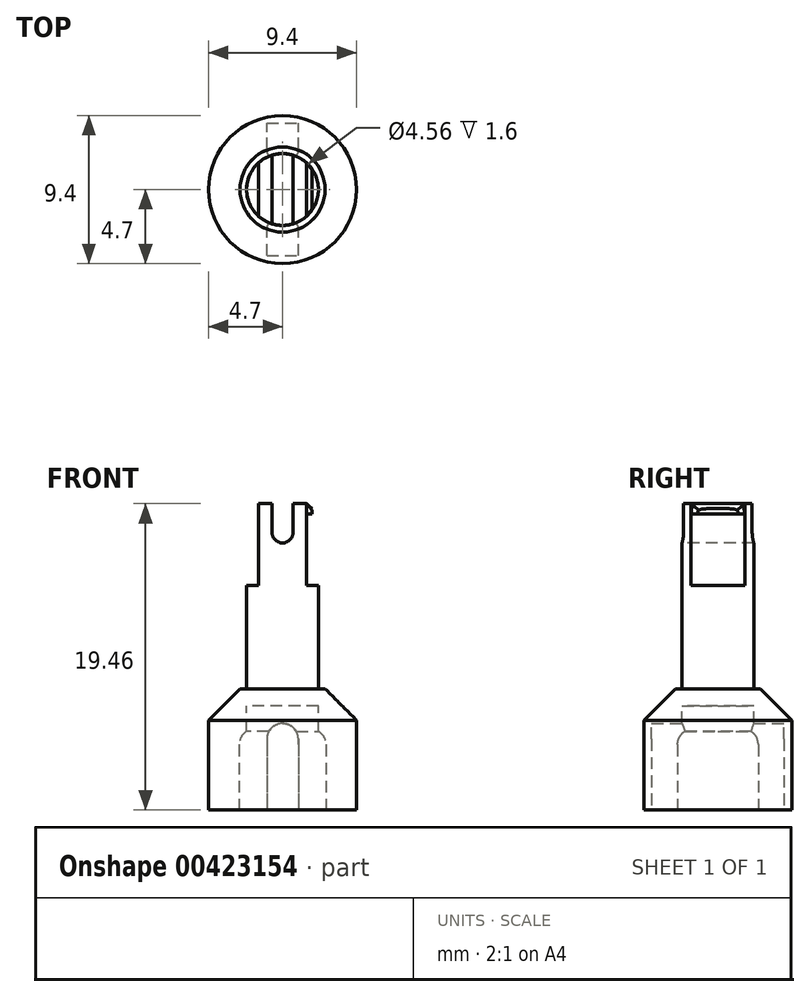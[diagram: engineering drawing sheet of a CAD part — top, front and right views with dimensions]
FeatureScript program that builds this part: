
annotation { "Feature Type Name" : "Feature", "Feature Type Description" : "" }
export const myFeature = defineFeature(function(context is Context, id is Id, definition is map)
    precondition{}
    {
        {
            assignVariable(context, id + "F0", {"variableType" : VariableType.LENGTH, "name" : "dogbone_cutout", "lengthValue" : 5.5 * mm});
        }
        {
            assignVariable(context, id + "F1", {"variableType" : VariableType.LENGTH, "name" : "shaft_length", "lengthValue" : 11.76 * mm});
        }
        {
            assignVariable(context, id + "F2", {"variableType" : VariableType.LENGTH, "name" : "outdrive_length", "lengthValue" : 7.7 * mm});
        }
        {
            assignVariable(context, id + "F3", {"variableType" : VariableType.LENGTH, "name" : "outdrive_depth", "lengthValue" : 6.6 * mm});
        }
        {
            assignVariable(context, id + "F4", {"variableType" : VariableType.LENGTH, "name" : "shaft_flat_length", "lengthValue" : 5.2 * mm});
        }
        {
            assignVariable(context, id + "F5", {"variableType" : VariableType.LENGTH, "name" : "flat_cutout_width", "lengthValue" : 1.35 * mm});
        }
        {
            assignVariable(context, id + "F6", {"variableType" : VariableType.LENGTH, "name" : "flat_cutout_depth", "lengthValue" : 2.5 * mm});
        }
        {
            assignVariable(context, id + "F7", {"variableType" : VariableType.LENGTH, "name" : "chamfer_length", "lengthValue" : 2 * mm});
        }
        {
            var Q0;
            Q0=qCreatedBy(makeId("Top.planeOp"),FACE);
            var sketch = newSketch(context, id + "F8", { "sketchPlane" : qUnion([Q0])});
            skCircle(sketch, "E0", {"center": v(0, 0) * mm, "radius": 4.7 * mm});
            skCircle(sketch, "E1", {"center": v(0, 0) * mm, "radius": 2.28 * mm});
            skSolve(sketch);
        }
        {
            var Q0;
            Q0=makeQuery(id+"F8.imprint","IMPRINT",FACE,{"disambiguationData":[TD([[makeQuery(id+"F8.imprint","IMPRINT",EDGE,{"derivedFrom":sQuery(id+"F8.wireOp",EDGE,"E1")}),1.0]])]});
            extrude(context, id + "F9", {"entities" : qUnion([Q0]), "depth" : getVariable(context, 'shaft_length'), "offsetDistance" : 25 * mm, "hasSecondDirection" : true, "secondDirectionOppositeDirection" : true, "secondDirectionDepth" : getVariable(context, 'outdrive_length') - getVariable(context, 'outdrive_depth')});
        }
        {
            var Q0;
            Q0=makeQuery(id+"F8.imprint","IMPRINT",FACE,{"disambiguationData":[TD([[makeQuery(id+"F8.imprint","IMPRINT",EDGE,{"derivedFrom":sQuery(id+"F8.wireOp",EDGE,"E0")}),1.0]])]});
            extrude(context, id + "F10", {"entities" : qUnion([Q0]), "operationType" : NewBodyOperationType.ADD, "oppositeDirection" : true, "depth" : getVariable(context, 'outdrive_length'), "offsetDistance" : 25 * mm});
        }
        {
            var Q0;
            Q0=makeQuery(id+"F10.opExtrude","CAP_EDGE",EDGE,{"disambiguationData":[OSD([sQuery(id+"F8.wireOp",EDGE,"E0")])],"isStart":true});
            chamfer(context, id + "F11", {"entities" : qUnion([Q0]), "width" : getVariable(context, 'chamfer_length'), "tangentPropagation" : true});
        }
        {
            var Q0;
            Q0=makeQuery(id+"F9.opExtrude","CAP_FACE",FACE,{"disambiguationData":[OSD([sQuery(id+"F8.wireOp",EDGE,"E1")])],"isStart":false});
            var sketch = newSketch(context, id + "F12", { "sketchPlane" : qUnion([Q0])});
            skLineSegment(sketch, "E2.bottom", {"start": v(1.51, 4.45) * mm, "end": v(-1.51, 4.45) * mm, "construction": true});
            skLineSegment(sketch, "E2.top", {"start": v(1.51, -4.45) * mm, "end": v(-1.51, -4.45) * mm, "construction": true});
            skLineSegment(sketch, "E2.left", {"start": v(1.51, 4.45) * mm, "end": v(1.51, -4.45) * mm});
            skLineSegment(sketch, "E2.right", {"start": v(-1.51, 4.45) * mm, "end": v(-1.51, -4.45) * mm});
            skPoint(sketch, "E2.middle", {"position": v(0, 0) * mm});
            skLineSegment(sketch, "E3", {"start": v(1.51, 4.45) * mm, "end": v(3.52, 4.45) * mm});
            skLineSegment(sketch, "E4", {"start": v(3.52, 4.45) * mm, "end": v(3.52, -4.43) * mm});
            skLineSegment(sketch, "E5", {"start": v(3.52, -4.43) * mm, "end": v(1.51, -4.45) * mm});
            skLineSegment(sketch, "E6.MirrorCS", {"start": v(-1.51, 4.45) * mm, "end": v(-3.52, 4.45) * mm});
            skLineSegment(sketch, "E7.MirrorCS", {"start": v(-3.52, 4.45) * mm, "end": v(-3.52, -4.43) * mm});
            skLineSegment(sketch, "E8.MirrorCS", {"start": v(-3.52, -4.43) * mm, "end": v(-1.51, -4.45) * mm});
            skSolve(sketch);
        }
        {
            var Q0;
            Q0 = qSketchRegion(id + "F12", true);
            extrude(context, id + "F13", {"entities" : qUnion([Q0]), "operationType" : NewBodyOperationType.REMOVE, "oppositeDirection" : true, "depth" : getVariable(context, 'shaft_flat_length'), "offsetDistance" : 25 * mm});
        }
        {
            var Q0;
            Q0=makeQuery(id+"F9.opExtrude","CAP_FACE",FACE,{"disambiguationData":[OSD([sQuery(id+"F8.wireOp",EDGE,"E1")])],"isStart":false});
            var sketch = newSketch(context, id + "F14", { "sketchPlane" : qUnion([Q0])});
            skLineSegment(sketch, "E9.bottom", {"start": v(-0.68, 4.65) * mm, "end": v(0.68, 4.65) * mm});
            skLineSegment(sketch, "E9.top", {"start": v(-0.68, -4.65) * mm, "end": v(0.68, -4.65) * mm});
            skLineSegment(sketch, "E9.left", {"start": v(-0.68, 4.65) * mm, "end": v(-0.68, -4.65) * mm});
            skLineSegment(sketch, "E9.right", {"start": v(0.68, 4.65) * mm, "end": v(0.68, -4.65) * mm});
            skPoint(sketch, "E9.middle", {"position": v(0, 0) * mm});
            skSolve(sketch);
        }
        {
            var Q0;
            Q0 = qSketchRegion(id + "F14", true);
            extrude(context, id + "F15", {"entities" : qUnion([Q0]), "operationType" : NewBodyOperationType.REMOVE, "oppositeDirection" : true, "depth" : getVariable(context, 'flat_cutout_depth'), "offsetDistance" : 25 * mm});
        }
        {
            var Q0;
            Q0=makeQuery(id+"F15.boolean.opBoolean","COPY",EDGE,{"derivedFrom":makeQuery(id+"F15.opExtrude","CAP_EDGE",EDGE,{"disambiguationData":[OSD([sQuery(id+"F14.wireOp",EDGE,"E9.left")])],"isStart":false})});
            var Q1;
            Q1=makeQuery(id+"F15.boolean.opBoolean","COPY",EDGE,{"derivedFrom":makeQuery(id+"F15.opExtrude","CAP_EDGE",EDGE,{"disambiguationData":[OSD([sQuery(id+"F14.wireOp",EDGE,"E9.right")])],"isStart":false})});
            fillet(context, id + "F16", {"entities" : qUnion([Q0, Q1]), "tangentPropagation" : true, "radius" : getVariable(context, 'flat_cutout_width') / 2, "defaultsChanged" : false, "vertexSettings" : [], "allowEdgeOverflow" : false});
        }
        {
            assignVariable(context, id + "F17", {"variableType" : VariableType.LENGTH, "name" : "flat_bump_offset", "lengthValue" : 0.65 * mm});
        }
        {
            var Q0;
            {var subQ0=sQuery(id+"F8.wireOp",EDGE,"E1");Q0=makeQuery(id+"F15.boolean.opBoolean","SPLIT",FACE,{"disambiguationData":[TD([makeQuery(id+"F13.boolean.opBoolean","COPY",FACE,{"derivedFrom":makeQuery(id+"F13.opExtrude","SWEPT_FACE",FACE,{"disambiguationData":[OSD([sQuery(id+"F12.wireOp",EDGE,"E2.left")])]})})])],"derivedFrom":makeQuery(id+"F9.opExtrude","CAP_FACE",FACE,{"disambiguationData":[OSD([subQ0])],"isStart":false})});}
            cPlane(context, id + "F18", {"entities" : qUnion([Q0]), "cplaneType" : CPlaneType.OFFSET, "offset" : getVariable(context, 'flat_bump_offset'), "oppositeDirection" : true, "width" : 150 * mm, "height" : 150 * mm});
        }
        {
            var Q0;
            Q0=qCreatedBy(id+"F18.planeOp",FACE);
            var sketch = newSketch(context, id + "F19", { "sketchPlane" : qUnion([Q0])});
            skArc(sketch, "E10", {"start": v(0.67, -2.18) * mm, "mid": v(2.28, 0) * mm, "end": v(0.68, 2.18) * mm});
            skLineSegment(sketch, "E11", {"start": v(0.67, 2.18) * mm, "end": v(0.68, -2.18) * mm});
            skArc(sketch, "E12.MirrorCS", {"start": v(-0.67, -2.18) * mm, "mid": v(-2.28, 0) * mm, "end": v(-0.68, 2.18) * mm});
            skLineSegment(sketch, "E13.MirrorCS", {"start": v(-0.67, 2.18) * mm, "end": v(-0.68, -2.18) * mm});
            skSolve(sketch);
        }
        {
            var Q0;
            Q0=makeQuery(id+"F19.imprint","IMPRINT",FACE,{"disambiguationData":[TD([[makeQuery(id+"F19.imprint","IMPRINT",EDGE,{"derivedFrom":sQuery(id+"F19.wireOp",EDGE,"E10")}),1.0]])]});
            var Q1;
            {var subQ0=sQuery(id+"F8.wireOp",EDGE,"E1");Q1=makeQuery(id+"F15.boolean.opBoolean","SPLIT",FACE,{"disambiguationData":[TD([makeQuery(id+"F13.boolean.opBoolean","COPY",FACE,{"derivedFrom":makeQuery(id+"F13.opExtrude","SWEPT_FACE",FACE,{"disambiguationData":[OSD([sQuery(id+"F12.wireOp",EDGE,"E2.left")])]})})])],"derivedFrom":makeQuery(id+"F9.opExtrude","CAP_FACE",FACE,{"disambiguationData":[OSD([subQ0])],"isStart":false})});}
            loft(context, id + "F20", {"operationType" : NewBodyOperationType.ADD, "sheetProfilesArray" : [{ "sheetProfileEntities" : qUnion([Q0]) }, { "sheetProfileEntities" : qUnion([Q1]) }]});
        }
        {
            var Q0;
            Q0=qCreatedBy(id+"F18.planeOp",FACE);
            var sketch = newSketch(context, id + "F21", { "sketchPlane" : qUnion([Q0])});
            skLineSegment(sketch, "E14.bottom", {"start": v(2.28, 1.95) * mm, "end": v(1.86, 1.95) * mm});
            skLineSegment(sketch, "E14.top", {"start": v(2.28, -1.95) * mm, "end": v(1.86, -1.95) * mm});
            skLineSegment(sketch, "E14.left", {"start": v(2.28, 1.95) * mm, "end": v(2.28, -1.95) * mm});
            skLineSegment(sketch, "E14.right", {"start": v(1.86, 1.95) * mm, "end": v(1.86, -1.95) * mm});
            skLineSegment(sketch, "E15.MirrorCS", {"start": v(-1.86, 1.95) * mm, "end": v(-1.86, -1.95) * mm});
            skLineSegment(sketch, "E16.MirrorCS", {"start": v(-2.28, 1.95) * mm, "end": v(-1.86, 1.95) * mm});
            skLineSegment(sketch, "E17.MirrorCS", {"start": v(-2.28, 1.95) * mm, "end": v(-2.28, -1.95) * mm});
            skLineSegment(sketch, "E18.MirrorCS", {"start": v(-2.28, -1.95) * mm, "end": v(-1.86, -1.95) * mm});
            skSolve(sketch);
        }
        {
            var Q0;
            Q0 = qSketchRegion(id + "F21", true);
            extrude(context, id + "F22", {"entities" : qUnion([Q0]), "operationType" : NewBodyOperationType.REMOVE, "depth" : 25 * mm, "offsetDistance" : 25 * mm});
        }
        {
            assignVariable(context, id + "F23", {"variableType" : VariableType.LENGTH, "name" : "dogbone_pin_od", "lengthValue" : 2 * mm});
        }
        {
            var Q0;
            Q0=makeQuery(id+"F10.opExtrude","CAP_FACE",FACE,{"disambiguationData":[OSD([sQuery(id+"F8.wireOp",EDGE,"E0"),sQuery(id+"F8.wireOp",EDGE,"E1")])],"isStart":false});
            var sketch = newSketch(context, id + "F24", { "sketchPlane" : qUnion([Q0])});
            skCircle(sketch, "E19", {"center": v(0, 0) * mm, "radius": 2.75 * mm});
            skSolve(sketch);
        }
        {
            var Q0;
            Q0=makeQuery(id+"F24.imprint","IMPRINT",FACE,{"disambiguationData":[TD([[makeQuery(id+"F24.imprint","IMPRINT",EDGE,{"derivedFrom":sQuery(id+"F24.wireOp",EDGE,"E19")}),1.0]])]});
            extrude(context, id + "F25", {"entities" : qUnion([Q0]), "operationType" : NewBodyOperationType.REMOVE, "oppositeDirection" : true, "depth" : 5 * mm, "offsetDistance" : 25 * mm});
        }
        {
            var Q0;
            Q0=makeQuery(id+"F10.opExtrude","CAP_FACE",FACE,{"disambiguationData":[OSD([sQuery(id+"F8.wireOp",EDGE,"E0"),sQuery(id+"F8.wireOp",EDGE,"E1")])],"isStart":false});
            var sketch = newSketch(context, id + "F26", { "sketchPlane" : qUnion([Q0])});
            skLineSegment(sketch, "E20.bottom", {"start": v(-1, 4.2) * mm, "end": v(1, 4.2) * mm});
            skLineSegment(sketch, "E20.top", {"start": v(-1, -4.2) * mm, "end": v(1, -4.2) * mm});
            skLineSegment(sketch, "E20.left", {"start": v(-1, 4.2) * mm, "end": v(-1, -4.2) * mm});
            skLineSegment(sketch, "E20.right", {"start": v(1, 4.2) * mm, "end": v(1, -4.2) * mm});
            skPoint(sketch, "E20.middle", {"position": v(0, 0) * mm});
            skSolve(sketch);
        }
        {
            var Q0;
            Q0 = qSketchRegion(id + "F26", true);
            extrude(context, id + "F27", {"entities" : qUnion([Q0]), "operationType" : NewBodyOperationType.REMOVE, "oppositeDirection" : true, "depth" : getVariable(context, 'dogbone_cutout'), "offsetDistance" : 25 * mm});
        }
        {
            var Q0;
            Q0=makeQuery(id+"F27.boolean.opBoolean","COPY",EDGE,{"disambiguationData":[OD(1.0)],"derivedFrom":makeQuery(id+"F27.opExtrude","CAP_EDGE",EDGE,{"disambiguationData":[OSD([sQuery(id+"F26.wireOp",EDGE,"E20.left")])],"isStart":false})});
            var Q1;
            Q1=makeQuery(id+"F27.boolean.opBoolean","COPY",EDGE,{"disambiguationData":[OD(0.0)],"derivedFrom":makeQuery(id+"F27.opExtrude","CAP_EDGE",EDGE,{"disambiguationData":[OSD([sQuery(id+"F26.wireOp",EDGE,"E20.left")])],"isStart":false})});
            var Q2;
            Q2=makeQuery(id+"F27.boolean.opBoolean","COPY",EDGE,{"disambiguationData":[OD(0.0)],"derivedFrom":makeQuery(id+"F27.opExtrude","CAP_EDGE",EDGE,{"disambiguationData":[OSD([sQuery(id+"F26.wireOp",EDGE,"E20.right")])],"isStart":false})});
            var Q3;
            Q3=makeQuery(id+"F27.boolean.opBoolean","COPY",EDGE,{"disambiguationData":[OD(1.0)],"derivedFrom":makeQuery(id+"F27.opExtrude","CAP_EDGE",EDGE,{"disambiguationData":[OSD([sQuery(id+"F26.wireOp",EDGE,"E20.right")])],"isStart":false})});
            var Q4;
            Q4=makeQuery(id+"F9.opExtrude","CAP_EDGE",EDGE,{"disambiguationData":[OSD([sQuery(id+"F8.wireOp",EDGE,"E1")])],"isStart":true});
            fillet(context, id + "F28", {"entities" : qUnion([Q0, Q1, Q2, Q3, Q4]), "tangentPropagation" : true, "radius" : getVariable(context, 'dogbone_pin_od') / 2, "defaultsChanged" : false, "vertexSettings" : [], "allowEdgeOverflow" : false});
        }
        {
            var Q0;
            {var subQ0=sQuery(id+"F24.wireOp",EDGE,"E19");Q0=makeQuery(id+"F27.boolean.opBoolean","SPLIT",EDGE,{"disambiguationData":[TD([makeQuery(id+"F27.opExtrude","SWEPT_FACE",FACE,{"disambiguationData":[OSD([sQuery(id+"F26.wireOp",EDGE,"E20.right")])]})])],"derivedFrom":makeQuery(id+"F25.boolean.opBoolean","COPY",EDGE,{"derivedFrom":makeQuery(id+"F25.opExtrude","CAP_EDGE",EDGE,{"disambiguationData":[OSD([subQ0])],"isStart":false})})});}
            var Q1;
            {var subQ0=sQuery(id+"F24.wireOp",EDGE,"E19");Q1=makeQuery(id+"F27.boolean.opBoolean","SPLIT",EDGE,{"disambiguationData":[TD([makeQuery(id+"F27.opExtrude","SWEPT_FACE",FACE,{"disambiguationData":[OSD([sQuery(id+"F26.wireOp",EDGE,"E20.left")])]})])],"derivedFrom":makeQuery(id+"F25.boolean.opBoolean","COPY",EDGE,{"derivedFrom":makeQuery(id+"F25.opExtrude","CAP_EDGE",EDGE,{"disambiguationData":[OSD([subQ0])],"isStart":false})})});}
            fillet(context, id + "F29", {"entities" : qUnion([Q0, Q1]), "tangentPropagation" : true, "radius" : 1 * mm, "defaultsChanged" : true, "vertexSettings" : [], "allowEdgeOverflow" : false});
        }
    });
